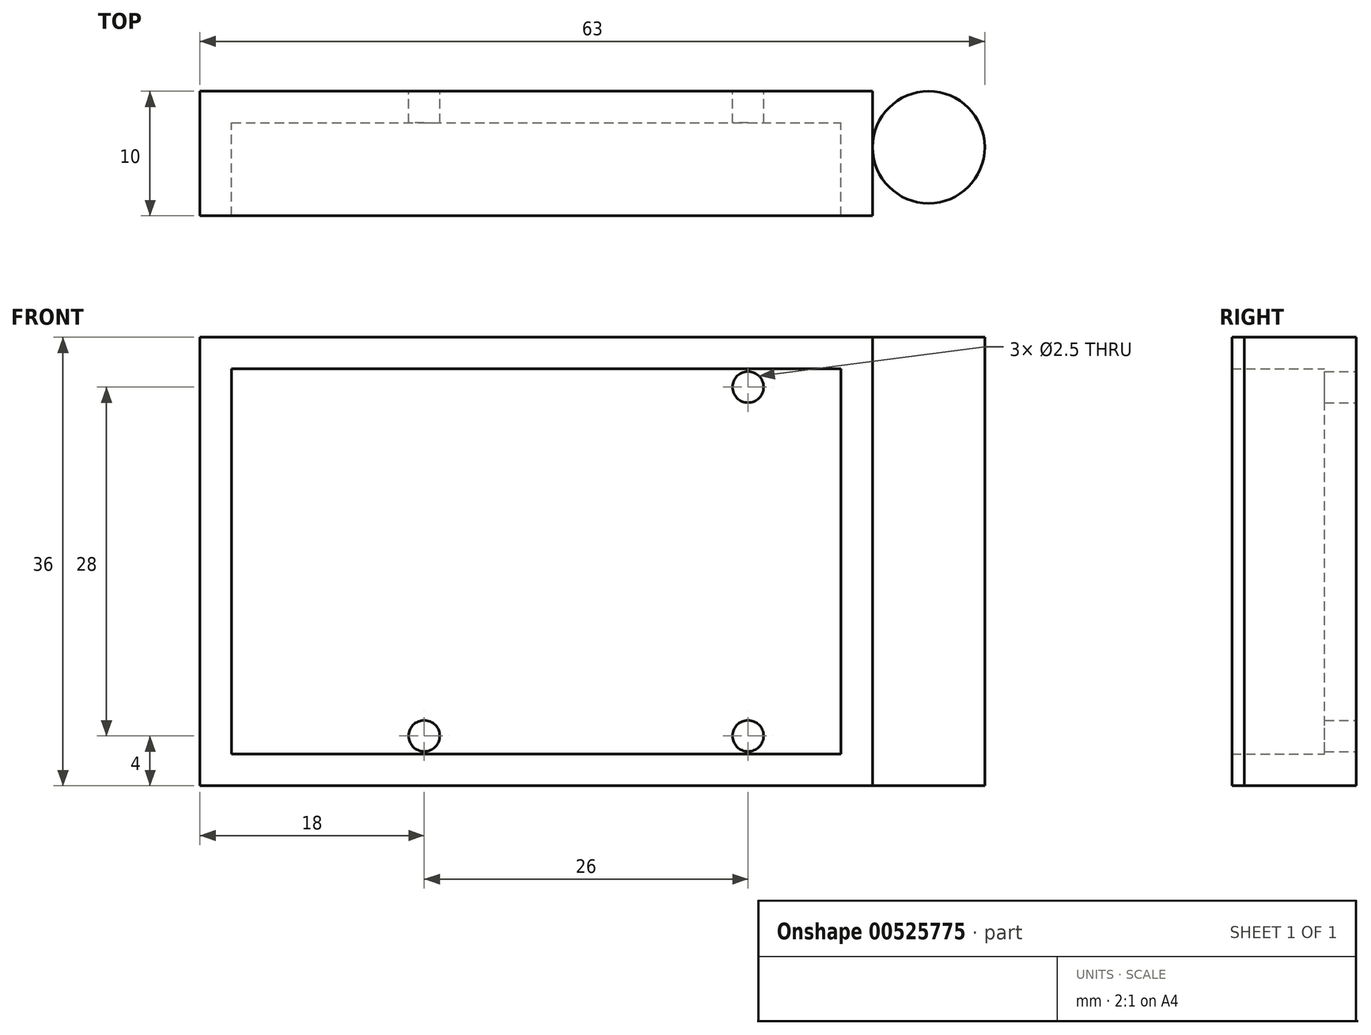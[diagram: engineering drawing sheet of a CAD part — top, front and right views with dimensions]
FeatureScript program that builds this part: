
annotation { "Feature Type Name" : "Feature", "Feature Type Description" : "" }
export const myFeature = defineFeature(function(context is Context, id is Id, definition is map)
    precondition{}
    {
        {
            var Q0;
            Q0=qCreatedBy(makeId("Front.planeOp"),FACE);
            var sketch = newSketch(context, id + "F0", { "sketchPlane" : qUnion([Q0])});
            skLineSegment(sketch, "E0.bottom", {"start": v(0, 0) * mm, "end": v(54, 0) * mm});
            skLineSegment(sketch, "E0.top", {"start": v(0, 36) * mm, "end": v(54, 36) * mm});
            skLineSegment(sketch, "E0.left", {"start": v(0, 0) * mm, "end": v(0, 36) * mm});
            skLineSegment(sketch, "E0.right", {"start": v(54, 0) * mm, "end": v(54, 36) * mm});
            skLineSegment(sketch, "E1", {"start": v(18, 36) * mm, "end": v(18, 0) * mm});
            skLineSegment(sketch, "E2", {"start": v(44, 36) * mm, "end": v(44, 0) * mm});
            skLineSegment(sketch, "E3", {"start": v(54, 32) * mm, "end": v(0, 32) * mm});
            skLineSegment(sketch, "E4", {"start": v(54, 4) * mm, "end": v(0, 4) * mm});
            skPoint(sketch, "E5", {"position": v(18, 32) * mm});
            skPoint(sketch, "E6", {"position": v(44, 32) * mm});
            skPoint(sketch, "E7", {"position": v(44, 4) * mm});
            skPoint(sketch, "E8", {"position": v(18, 4) * mm});
            skSolve(sketch);
        }
        {
            var Q0;
            Q0=qCreatedBy(makeId("Front.planeOp"),FACE);
            var sketch = newSketch(context, id + "F1", { "sketchPlane" : qUnion([Q0])});
            skLineSegment(sketch, "E9.bottom", {"start": v(0, 0) * mm, "end": v(54, 0) * mm});
            skLineSegment(sketch, "E9.top", {"start": v(0, 36) * mm, "end": v(54, 36) * mm});
            skLineSegment(sketch, "E9.left", {"start": v(0, 0) * mm, "end": v(0, 36) * mm});
            skLineSegment(sketch, "E9.right", {"start": v(54, 0) * mm, "end": v(54, 36) * mm});
            skSolve(sketch);
        }
        {
            var Q0;
            Q0 = qSketchRegion(id + "F1", true);
            extrude(context, id + "F2", {"entities" : qUnion([Q0]), "depth" : 10 * mm, "offsetDistance" : 25.4 * mm});
        }
        {
            var Q0;
            Q0=makeQuery(id+"F2.opExtrude","CAP_FACE",FACE,{"disambiguationData":[OSD([sQuery(id+"F1.wireOp",EDGE,"E9.bottom"),sQuery(id+"F1.wireOp",EDGE,"E9.top"),sQuery(id+"F1.wireOp",EDGE,"E9.left"),sQuery(id+"F1.wireOp",EDGE,"E9.right")])],"isStart":false});
            shell(context, id + "F3", {"entities" : qUnion([Q0]), "thickness" : 2.54 * mm});
        }
        {
            var Q0;
            Q0=sQuery(id+"F0.wireOp",VERTEX,"E7");
            var Q1;
            Q1=sQuery(id+"F0.wireOp",VERTEX,"E6");
            var Q2;
            Q2=sQuery(id+"F0.wireOp",VERTEX,"E8");
            var Q3;
            Q3=makeQuery(id+"F2.opExtrude","SWEPT_BODY",BODY,{"disambiguationData":[OSD([sQuery(id+"F1.wireOp",EDGE,"E9.bottom"),sQuery(id+"F1.wireOp",EDGE,"E9.top"),sQuery(id+"F1.wireOp",EDGE,"E9.left"),sQuery(id+"F1.wireOp",EDGE,"E9.right")])]});
            hole(context, id + "F4", {"style" : HoleStyle.SIMPLE, "endStyle" : HoleEndStyle.THROUGH, "oppositeDirection" : true, "holeDiameter" : 2.5 * mm, "isTappedThrough" : true, "tappedDepth" : 12.7 * mm, "tapClearance" : 3, "locations" : qUnion([Q0, Q1, Q2]), "scope" : qUnion([Q3])});
        }
        {
            var Q0;
            Q0=qCreatedBy(makeId("Top.planeOp"),FACE);
            var sketch = newSketch(context, id + "F5", { "sketchPlane" : qUnion([Q0])});
            skCircle(sketch, "E10", {"center": v(58.5, -4.5) * mm, "radius": 4.5 * mm});
            skSolve(sketch);
        }
        {
            var Q0;
            Q0=makeQuery(id+"F5.imprint","IMPRINT",FACE,{"disambiguationData":[TD([[makeQuery(id+"F5.imprint","IMPRINT",EDGE,{"derivedFrom":sQuery(id+"F5.wireOp",EDGE,"E10")}),1.0]])]});
            var Q1;
            Q1=makeQuery(id+"F2.opExtrude","SWEPT_FACE",FACE,{"disambiguationData":[OSD([sQuery(id+"F1.wireOp",EDGE,"E9.top")])]});
            extrude(context, id + "F6", {"entities" : qUnion([Q0]), "operationType" : NewBodyOperationType.ADD, "endBound" : BoundingType.UP_TO_SURFACE, "depth" : 25.4 * mm, "endBoundEntityFace" : qUnion([Q1]), "offsetDistance" : 25.4 * mm});
        }
    });
